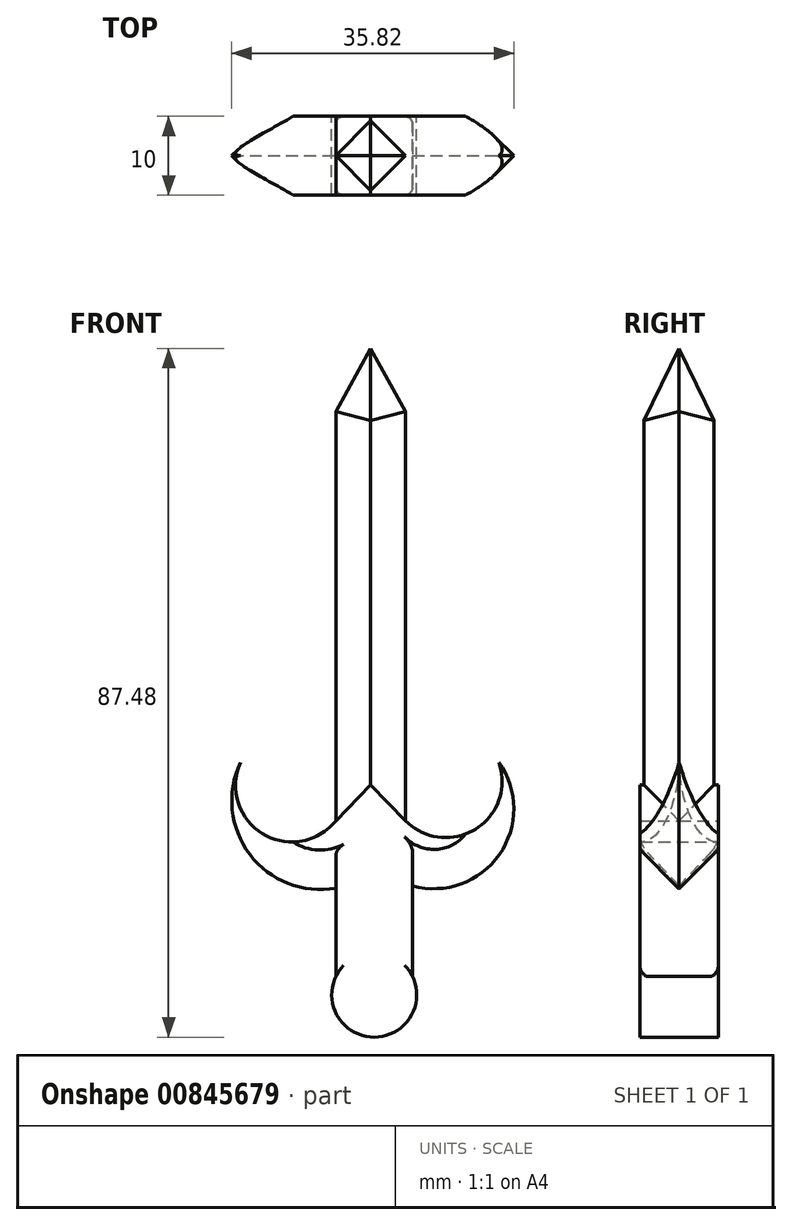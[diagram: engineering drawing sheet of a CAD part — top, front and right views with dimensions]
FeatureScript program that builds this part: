
annotation { "Feature Type Name" : "Feature", "Feature Type Description" : "" }
export const myFeature = defineFeature(function(context is Context, id is Id, definition is map)
    precondition{}
    {
        {
            var Q0;
            Q0=qCreatedBy(makeId("Front.planeOp"),FACE);
            var sketch = newSketch(context, id + "F0", { "sketchPlane" : qUnion([Q0])});
            skLineSegment(sketch, "E0", {"start": v(39.74, 5.9) * mm, "end": v(39.74, 57.92) * mm});
            skLineSegment(sketch, "E1", {"start": v(30.88, 5.9) * mm, "end": v(30.88, 57.92) * mm});
            skArc(sketch, "E2", {"start": v(39.74, 5.9) * mm, "mid": v(48.65, 4.84) * mm, "end": v(51.6, 13.31) * mm});
            skArc(sketch, "E3", {"start": v(18.76, 13.3) * mm, "mid": v(21.57, 4.26) * mm, "end": v(30.88, 5.9) * mm});
            skArc(sketch, "E4", {"start": v(40.63, -2.37) * mm, "mid": v(51.65, 1.6) * mm, "end": v(51.6, 13.31) * mm});
            skArc(sketch, "E5", {"start": v(18.76, 13.3) * mm, "mid": v(19.96, 1.62) * mm, "end": v(30.88, -2.66) * mm});
            skLineSegment(sketch, "E6", {"start": v(39.74, 57.92) * mm, "end": v(35.31, 65.9) * mm});
            skLineSegment(sketch, "E7", {"start": v(35.31, 65.9) * mm, "end": v(30.88, 57.92) * mm});
            skLineSegment(sketch, "E8", {"start": v(39.74, 5.9) * mm, "end": v(35.31, 10.44) * mm});
            skLineSegment(sketch, "E9", {"start": v(35.31, 10.44) * mm, "end": v(30.88, 5.9) * mm});
            skLineSegment(sketch, "E10", {"start": v(40.63, -2.37) * mm, "end": v(40.63, -13.89) * mm});
            skLineSegment(sketch, "E11", {"start": v(30.88, -2.66) * mm, "end": v(30.88, -13.89) * mm});
            skArc(sketch, "E12", {"start": v(30.88, -13.89) * mm, "mid": v(35.76, -21.6) * mm, "end": v(40.63, -13.89) * mm});
            skPoint(sketch, "E13.endSnap0", {"position": v(35.76, -21.6) * mm});
            skSolve(sketch);
        }
        {
            var Q0;
            Q0=makeQuery(id+"F0.imprint","IMPRINT",FACE,{"disambiguationData":[TD([[makeQuery(id+"F0.imprint","IMPRINT",EDGE,{"derivedFrom":sQuery(id+"F0.wireOp",EDGE,"E0")}),1.0]])]});
            extrude(context, id + "F1", {"entities" : qUnion([Q0]), "depth" : 10 * mm, "offsetDistance" : 25 * mm});
        }
        {
            var Q0;
            Q0=makeQuery(id+"F1.opExtrude","CAP_EDGE",EDGE,{"disambiguationData":[OSD([sQuery(id+"F0.wireOp",EDGE,"E6")])],"isStart":false});
            var Q1;
            Q1=makeQuery(id+"F1.opExtrude","CAP_EDGE",EDGE,{"disambiguationData":[OSD([sQuery(id+"F0.wireOp",EDGE,"E6")])],"isStart":true});
            var Q2;
            Q2=makeQuery(id+"F1.opExtrude","CAP_EDGE",EDGE,{"disambiguationData":[OSD([sQuery(id+"F0.wireOp",EDGE,"E7")])],"isStart":false});
            var Q3;
            Q3=makeQuery(id+"F1.opExtrude","CAP_EDGE",EDGE,{"disambiguationData":[OSD([sQuery(id+"F0.wireOp",EDGE,"E7")])],"isStart":true});
            chamfer(context, id + "F2", {"entities" : qUnion([Q0, Q1, Q2, Q3]), "width" : 5 * mm, "tangentPropagation" : true});
        }
        {
            var Q0;
            Q0=makeQuery(id+"F1.opExtrude","CAP_EDGE",EDGE,{"disambiguationData":[OSD([sQuery(id+"F0.wireOp",EDGE,"E1")])],"isStart":true});
            var Q1;
            Q1=makeQuery(id+"F1.opExtrude","CAP_EDGE",EDGE,{"disambiguationData":[OSD([sQuery(id+"F0.wireOp",EDGE,"E1")])],"isStart":false});
            var Q2;
            Q2=makeQuery(id+"F1.opExtrude","CAP_EDGE",EDGE,{"disambiguationData":[OSD([sQuery(id+"F0.wireOp",EDGE,"E0")])],"isStart":false});
            var Q3;
            Q3=makeQuery(id+"F1.opExtrude","CAP_EDGE",EDGE,{"disambiguationData":[OSD([sQuery(id+"F0.wireOp",EDGE,"E0")])],"isStart":true});
            chamfer(context, id + "F3", {"entities" : qUnion([Q0, Q1, Q2, Q3]), "width" : 5 * mm, "tangentPropagation" : true});
        }
        {
            var Q0;
            Q0=makeQuery(id+"F0.imprint","IMPRINT",FACE,{"disambiguationData":[TD([[makeQuery(id+"F0.imprint","IMPRINT",EDGE,{"derivedFrom":sQuery(id+"F0.wireOp",EDGE,"E2")}),-1.0]])]});
            extrude(context, id + "F4", {"entities" : qUnion([Q0]), "operationType" : NewBodyOperationType.ADD, "depth" : 10 * mm, "offsetDistance" : 25 * mm});
        }
        {
            var Q0;
            Q0=makeQuery(id+"F4.opExtrude","CAP_EDGE",EDGE,{"disambiguationData":[OSD([sQuery(id+"F0.wireOp",EDGE,"E5")])],"isStart":false});
            var Q1;
            Q1=makeQuery(id+"F4.opExtrude","CAP_EDGE",EDGE,{"disambiguationData":[OSD([sQuery(id+"F0.wireOp",EDGE,"E4")])],"isStart":false});
            chamfer(context, id + "F5", {"entities" : qUnion([Q0, Q1]), "width" : 5 * mm, "tangentPropagation" : true});
        }
        {
            var Q0;
            Q0=makeQuery(id+"F4.opExtrude","CAP_EDGE",EDGE,{"disambiguationData":[OSD([sQuery(id+"F0.wireOp",EDGE,"E4")])],"isStart":true});
            var Q1;
            Q1=makeQuery(id+"F4.opExtrude","CAP_EDGE",EDGE,{"disambiguationData":[OSD([sQuery(id+"F0.wireOp",EDGE,"E5")])],"isStart":true});
            chamfer(context, id + "F6", {"entities" : qUnion([Q0, Q1]), "width" : 5 * mm, "tangentPropagation" : true});
        }
        {
            var Q0;
            Q0=makeQuery(id+"F4.opExtrude","CAP_EDGE",EDGE,{"disambiguationData":[OSD([sQuery(id+"F0.wireOp",EDGE,"E10")])],"isStart":true});
            var Q1;
            Q1=makeQuery(id+"F4.opExtrude","CAP_EDGE",EDGE,{"disambiguationData":[OSD([sQuery(id+"F0.wireOp",EDGE,"E11")])],"isStart":true});
            var Q2;
            Q2=makeQuery(id+"F4.opExtrude","CAP_EDGE",EDGE,{"disambiguationData":[OSD([sQuery(id+"F0.wireOp",EDGE,"E10")])],"isStart":false});
            var Q3;
            Q3=makeQuery(id+"F4.opExtrude","CAP_EDGE",EDGE,{"disambiguationData":[OSD([sQuery(id+"F0.wireOp",EDGE,"E11")])],"isStart":false});
            fillet(context, id + "F7", {"entities" : qUnion([Q0, Q1, Q2, Q3]), "radius" : 1 * mm, "tangentPropagation" : true, "allowEdgeOverflow" : false});
        }
    });
